# Revit family: HUNTER_ACC-1200 Metal Pedestal
name_source: partatom
category: Electrical Equipment
revit_build: Autodesk Revit 2017 (Build: 20160225_1515(x64)
units: mm (PartAtom-declared; Revit-internal decimal feet)

## family parameters
Always vertical = Yes
Cut with Voids When Loaded = No
OmniClass Number = 23.35.25.21
Panel Configuration = One Column
Part Type = Panelboard
Room Calculation Point = No
Round Connector Dimension = Use Diameter
Shared = Yes
Work Plane-Based = Yes

## types (2) — shared parameters
Assembly Code = D5090900
Current = 2 A
Decoders = Expandable Up to 99 with Decoders
Default Elevation = 1219 mm
Expansion Module = A2M-600 (6 Stations plug-in) Expansion Module
Input Voltage = 120 V
Keynote = 328423.04
Manufacturer = Hunter® Industries
Number of Sensor Inputs = 4+ Dedicated Flow Input
Output Voltage = 24 V
Panel Type = Modular
Power = 240 VA
Power Factor = 1
Protection Rating = IP56
Sensor Input = 4 + Flow
Stations = 12 Stations base count expandable to 42 Stations
Transformer Output = 24VAC, 4.0A
Type Comments = Hunter’s Flagship Controller
Type Image = <None>
URL = https://www.hunterindustries.com

## per-type parameters (varying)
| type | ACC-1200 | ACC-1200-SS | Description | Model | Pedestal Material |
| ACC-1200 with ACC-PED | Yes | No | 12-Station base unit , Pedestal mounted controller, expandable to 42 stations, with Metal enclsoure and pedestal | ACC-1200 / ACC-1800 / ACC-2400 / ACC-3000 / ACC-3600 / ACC-4200 with ACC-PED | Hunter® Metal Grey |
| ACC-1200-SS with PED-SS | No | Yes | 12-Station base unit , Pedestal mounted controller, expandable to 42 stations, with Stainless steel enclosure and pedestal | ACC-1200-SS / ACC-1800-SS / ACC- 2400-SS / ACC-3000-SS / ACC-3600-SS / ACC-4200-SS with PED-SS | Hunter® Stainless Steel |

## geometry (parser evidence)
native form markers: Sweep x7
no freeform markers — native parametric forms only
